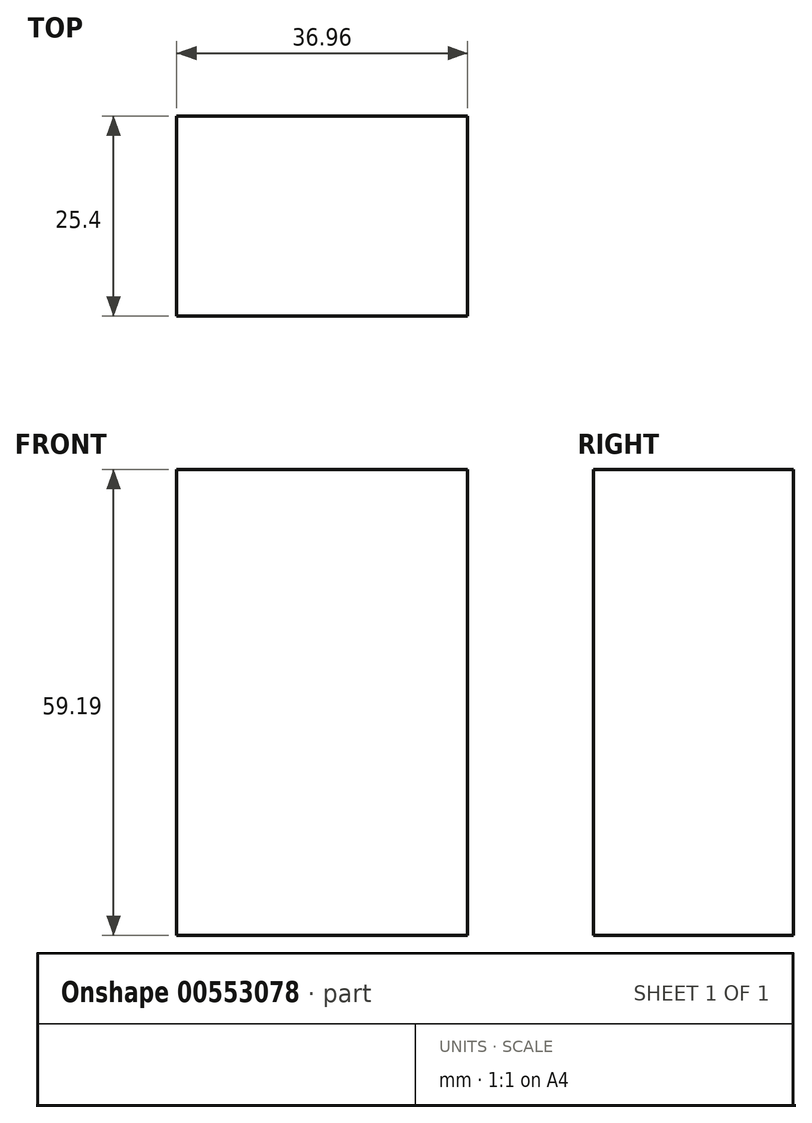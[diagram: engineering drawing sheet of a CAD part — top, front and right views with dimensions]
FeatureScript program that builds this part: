
annotation { "Feature Type Name" : "Feature", "Feature Type Description" : "" }
export const myFeature = defineFeature(function(context is Context, id is Id, definition is map)
    precondition{}
    {
        {
            var Q0;
            Q0=qCreatedBy(makeId("Front.planeOp"),FACE);
            var sketch = newSketch(context, id + "F0", { "sketchPlane" : qUnion([Q0])});
            skLineSegment(sketch, "E0.bottom", {"start": v(-166.85, 49.5) * mm, "end": v(-87.83, 49.5) * mm});
            skLineSegment(sketch, "E0.top", {"start": v(-166.85, 32.64) * mm, "end": v(-87.83, 32.64) * mm});
            skLineSegment(sketch, "E0.left", {"start": v(-166.85, 49.5) * mm, "end": v(-166.85, 32.64) * mm});
            skLineSegment(sketch, "E0.right", {"start": v(-87.83, 49.5) * mm, "end": v(-87.83, 32.64) * mm});
            skLineSegment(sketch, "E1.bottom", {"start": v(-47.14, 68.8) * mm, "end": v(-27.47, 68.8) * mm});
            skLineSegment(sketch, "E1.top", {"start": v(-47.14, 27.68) * mm, "end": v(-27.47, 27.68) * mm});
            skLineSegment(sketch, "E1.left", {"start": v(-47.14, 68.8) * mm, "end": v(-47.14, 27.68) * mm});
            skLineSegment(sketch, "E1.right", {"start": v(-27.47, 68.8) * mm, "end": v(-27.47, 27.68) * mm});
            skLineSegment(sketch, "E2.bottom", {"start": v(6.1, 57.72) * mm, "end": v(41.03, 57.72) * mm});
            skLineSegment(sketch, "E2.top", {"start": v(6.1, -51.57) * mm, "end": v(41.03, -51.57) * mm});
            skLineSegment(sketch, "E2.left", {"start": v(6.1, 57.72) * mm, "end": v(6.1, -51.57) * mm});
            skLineSegment(sketch, "E2.right", {"start": v(41.03, 57.72) * mm, "end": v(41.03, -51.57) * mm});
            skLineSegment(sketch, "E3.bottom", {"start": v(-95.97, -56.87) * mm, "end": v(-59, -56.87) * mm});
            skLineSegment(sketch, "E3.top", {"start": v(-95.97, -116.06) * mm, "end": v(-59, -116.06) * mm});
            skLineSegment(sketch, "E3.left", {"start": v(-95.97, -56.87) * mm, "end": v(-95.97, -116.06) * mm});
            skLineSegment(sketch, "E3.right", {"start": v(-59, -56.87) * mm, "end": v(-59, -116.06) * mm});
            skSolve(sketch);
        }
        {
            var Q0;
            Q0 = qSketchRegion(id + "F0", true);
            extrude(context, id + "F1", {"entities" : qUnion([Q0]), "depth" : 25.4 * mm, "offsetDistance" : 25.4 * mm});
        }
        {
            var Q0;
            Q0=makeQuery(id+"F1.opExtrude","SWEPT_BODY",BODY,{"disambiguationData":[OSD([sQuery(id+"F0.wireOp",EDGE,"E0.bottom"),sQuery(id+"F0.wireOp",EDGE,"E0.top"),sQuery(id+"F0.wireOp",EDGE,"E0.left"),sQuery(id+"F0.wireOp",EDGE,"E0.right")])]});
            var Q1;
            Q1=makeQuery(id+"F1.opExtrude","SWEPT_BODY",BODY,{"disambiguationData":[OSD([sQuery(id+"F0.wireOp",EDGE,"E2.bottom"),sQuery(id+"F0.wireOp",EDGE,"E2.top"),sQuery(id+"F0.wireOp",EDGE,"E2.left"),sQuery(id+"F0.wireOp",EDGE,"E2.right")])]});
            var Q2;
            Q2=makeQuery(id+"F1.opExtrude","SWEPT_BODY",BODY,{"disambiguationData":[OSD([sQuery(id+"F0.wireOp",EDGE,"E1.bottom"),sQuery(id+"F0.wireOp",EDGE,"E1.top"),sQuery(id+"F0.wireOp",EDGE,"E1.left"),sQuery(id+"F0.wireOp",EDGE,"E1.right")])]});
            deleteBodies(context, id + "F2", {"entities" : qUnion([Q0, Q1, Q2])});
        }
    });
